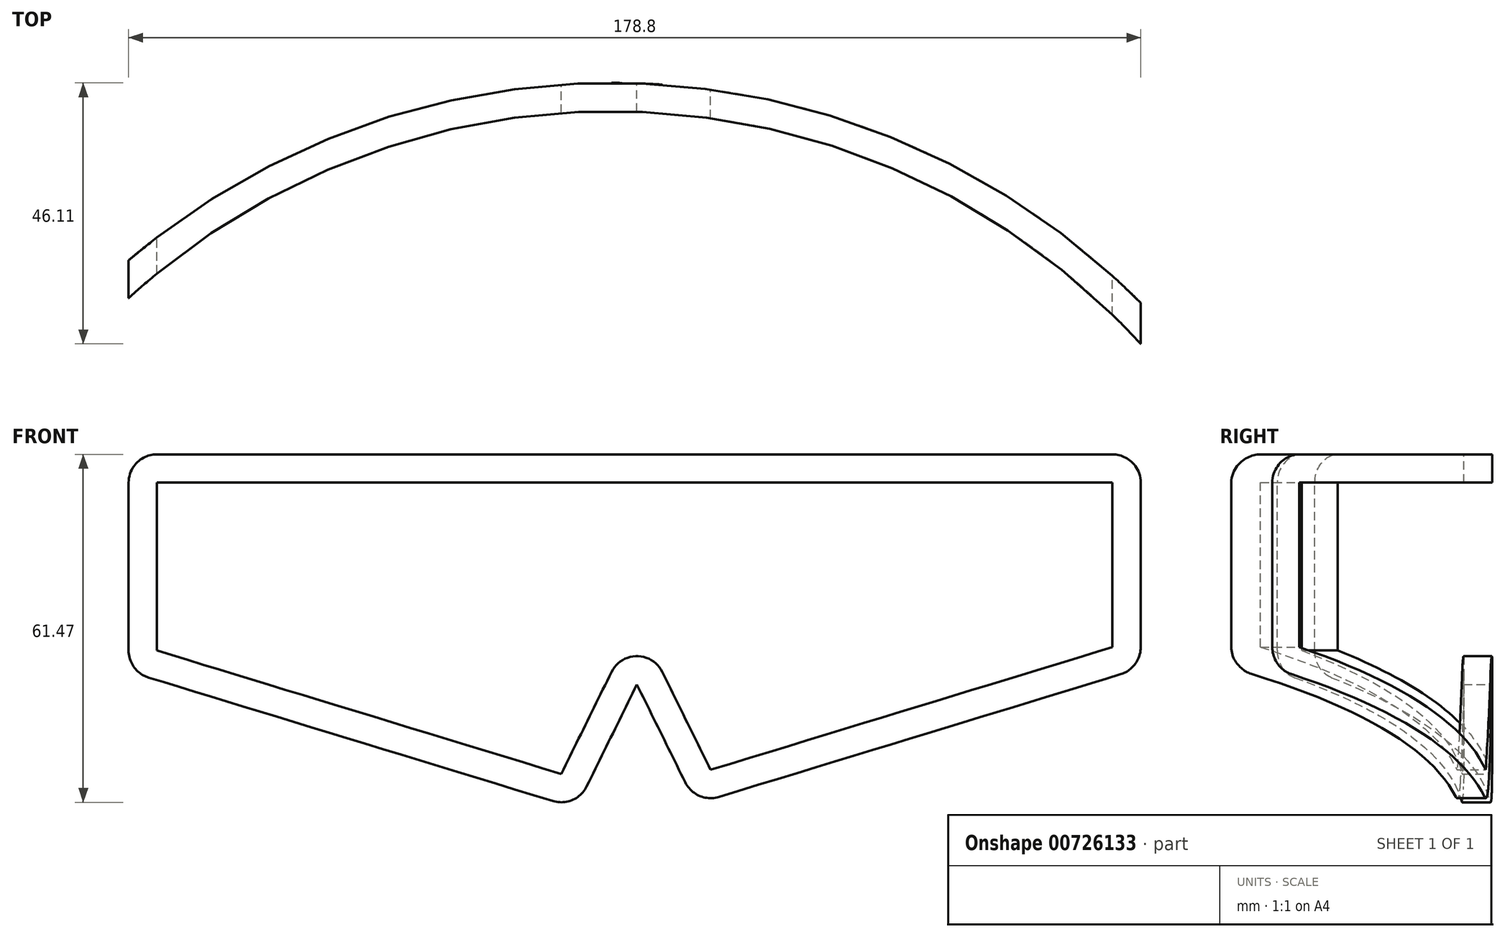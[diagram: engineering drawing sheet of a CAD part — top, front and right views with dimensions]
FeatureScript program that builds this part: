
annotation { "Feature Type Name" : "Feature", "Feature Type Description" : "" }
export const myFeature = defineFeature(function(context is Context, id is Id, definition is map)
    precondition{}
    {
        {
            var Q0;
            Q0=qCreatedBy(makeId("Front.planeOp"),FACE);
            var sketch = newSketch(context, id + "F0", { "sketchPlane" : qUnion([Q0])});
            skLineSegment(sketch, "E0.0", {"start": v(13.11, -10.56) * mm, "end": v(91.7, 13.44) * mm});
            skLineSegment(sketch, "E0.1", {"start": v(91.7, 13.44) * mm, "end": v(91.7, 51.2) * mm});
            skLineSegment(sketch, "E0.2", {"start": v(13.11, -10.56) * mm, "end": v(2.7, 10.55) * mm});
            skLineSegment(sketch, "E0.3", {"start": v(2.7, 51.2) * mm, "end": v(91.7, 51.2) * mm});
            skLineSegment(sketch, "E0.4", {"start": v(-8.07, -11.28) * mm, "end": v(2.7, 10.55) * mm});
            skLineSegment(sketch, "E0.5", {"start": v(-8.07, -11.28) * mm, "end": v(-87.1, 12.85) * mm});
            skLineSegment(sketch, "E0.6", {"start": v(-87.1, 12.85) * mm, "end": v(-87.1, 51.2) * mm});
            skLineSegment(sketch, "E0.7", {"start": v(2.7, 51.2) * mm, "end": v(-87.1, 51.2) * mm});
            skSolve(sketch);
        }
        {
            var Q0;
            Q0 = qSketchRegion(id + "F0", true);
            extrude(context, id + "F1", {"entities" : qUnion([Q0]), "depth" : 150 * mm, "offsetDistance" : 25 * mm});
        }
        {
            var Q0;
            Q0=makeQuery(id+"F1.opExtrude","CAP_FACE",FACE,{"disambiguationData":[OSD([sQuery(id+"F0.wireOp",EDGE,"E0.0"),sQuery(id+"F0.wireOp",EDGE,"E0.1"),sQuery(id+"F0.wireOp",EDGE,"E0.2"),sQuery(id+"F0.wireOp",EDGE,"E0.3"),sQuery(id+"F0.wireOp",EDGE,"E0.4"),sQuery(id+"F0.wireOp",EDGE,"E0.5"),sQuery(id+"F0.wireOp",EDGE,"E0.6"),sQuery(id+"F0.wireOp",EDGE,"E0.7")])],"isStart":true});
            var sketch = newSketch(context, id + "F2", { "sketchPlane" : qUnion([Q0])});
            skLineSegment(sketch, "E1.0", {"start": v(82.1, 16.55) * mm, "end": v(82.1, 46.2) * mm});
            skLineSegment(sketch, "E1.1", {"start": v(10.67, -5.26) * mm, "end": v(82.1, 16.55) * mm});
            skLineSegment(sketch, "E1.2", {"start": v(-86.7, 17.15) * mm, "end": v(-86.7, 46.2) * mm});
            skLineSegment(sketch, "E1.3", {"start": v(-15.72, -4.53) * mm, "end": v(-86.7, 17.15) * mm});
            skLineSegment(sketch, "E1.4", {"start": v(-15.72, -4.53) * mm, "end": v(-2.7, 21.86) * mm});
            skLineSegment(sketch, "E1.5", {"start": v(82.1, 46.2) * mm, "end": v(-86.7, 46.2) * mm});
            skLineSegment(sketch, "E1.6", {"start": v(10.67, -5.26) * mm, "end": v(-2.7, 21.86) * mm});
            skSolve(sketch);
        }
        {
            var Q0;
            Q0 = qSketchRegion(id + "F2", true);
            extrude(context, id + "F3", {"entities" : qUnion([Q0]), "operationType" : NewBodyOperationType.REMOVE, "oppositeDirection" : true, "depth" : 200 * mm, "offsetDistance" : 25 * mm});
        }
        {
            var Q0;
            Q0=makeQuery(id+"F1.opExtrude","SWEPT_FACE",FACE,{"disambiguationData":[OSD([sQuery(id+"F0.wireOp",EDGE,"E0.3"),sQuery(id+"F0.wireOp",EDGE,"E0.7")])]});
            var sketch = newSketch(context, id + "F4", { "sketchPlane" : qUnion([Q0])});
            skArc(sketch, "E2", {"start": v(110.16, -71.76) * mm, "mid": v(-2.51, -9.56) * mm, "end": v(-114.48, -73.03) * mm});
            skArc(sketch, "E3.0", {"start": v(105.92, -74.4) * mm, "mid": v(-2.48, -14.56) * mm, "end": v(-110.2, -75.62) * mm});
            skLineSegment(sketch, "E4", {"start": v(-114.48, -73.03) * mm, "end": v(-110.2, -75.62) * mm});
            skLineSegment(sketch, "E5", {"start": v(105.92, -74.4) * mm, "end": v(110.16, -71.76) * mm});
            skSolve(sketch);
        }
        {
            var Q0;
            Q0 = qSketchRegion(id + "F4", true);
            extrude(context, id + "F5", {"entities" : qUnion([Q0]), "operationType" : NewBodyOperationType.INTERSECT, "oppositeDirection" : true, "depth" : 100 * mm, "offsetDistance" : 25 * mm});
        }
        {
            var Q0;
            Q0=makeQuery(id+"F3.boolean.opBoolean","COPY",EDGE,{"derivedFrom":makeQuery(id+"F3.opExtrude","SWEPT_EDGE",EDGE,{"disambiguationData":[OSD([sQuery(id+"F2.wireOp",EDGE,"E1.4"),sQuery(id+"F2.wireOp",EDGE,"E1.6")])]})});
            fillet(context, id + "F6", {"entities" : qUnion([Q0]), "radius" : 5 * mm, "tangentPropagation" : true, "allowEdgeOverflow" : false});
        }
        {
            var Q0;
            Q0=makeQuery(id+"F1.opExtrude","SWEPT_EDGE",EDGE,{"disambiguationData":[OSD([sQuery(id+"F0.wireOp",EDGE,"E0.4"),sQuery(id+"F0.wireOp",EDGE,"E0.5")])]});
            fillet(context, id + "F7", {"entities" : qUnion([Q0]), "radius" : 5 * mm, "tangentPropagation" : true, "allowEdgeOverflow" : false});
        }
        {
            var Q0;
            Q0=makeQuery(id+"F1.opExtrude","SWEPT_EDGE",EDGE,{"disambiguationData":[OSD([sQuery(id+"F0.wireOp",EDGE,"E0.0"),sQuery(id+"F0.wireOp",EDGE,"E0.2")])]});
            fillet(context, id + "F8", {"entities" : qUnion([Q0]), "radius" : 5 * mm, "tangentPropagation" : true, "allowEdgeOverflow" : false});
        }
        {
            var Q0;
            Q0=makeQuery(id+"F1.opExtrude","SWEPT_EDGE",EDGE,{"disambiguationData":[OSD([sQuery(id+"F0.wireOp",EDGE,"E0.6"),sQuery(id+"F0.wireOp",EDGE,"E0.7")])]});
            fillet(context, id + "F9", {"entities" : qUnion([Q0]), "radius" : 5 * mm, "tangentPropagation" : true, "allowEdgeOverflow" : false});
        }
        {
            var Q0;
            Q0=makeQuery(id+"F1.opExtrude","SWEPT_EDGE",EDGE,{"disambiguationData":[OSD([sQuery(id+"F0.wireOp",EDGE,"E0.5"),sQuery(id+"F0.wireOp",EDGE,"E0.6")])]});
            fillet(context, id + "F10", {"entities" : qUnion([Q0]), "radius" : 5 * mm, "tangentPropagation" : true, "allowEdgeOverflow" : false});
        }
        {
            var Q0;
            Q0=makeQuery(id+"F1.opExtrude","SWEPT_EDGE",EDGE,{"disambiguationData":[OSD([sQuery(id+"F0.wireOp",EDGE,"E0.1"),sQuery(id+"F0.wireOp",EDGE,"E0.3")])]});
            fillet(context, id + "F11", {"entities" : qUnion([Q0]), "radius" : 5 * mm, "tangentPropagation" : true, "allowEdgeOverflow" : false});
        }
        {
            var Q0;
            Q0=makeQuery(id+"F1.opExtrude","SWEPT_EDGE",EDGE,{"disambiguationData":[OSD([sQuery(id+"F0.wireOp",EDGE,"E0.0"),sQuery(id+"F0.wireOp",EDGE,"E0.1")])]});
            fillet(context, id + "F12", {"entities" : qUnion([Q0]), "radius" : 5 * mm, "tangentPropagation" : true, "allowEdgeOverflow" : false});
        }
    });
